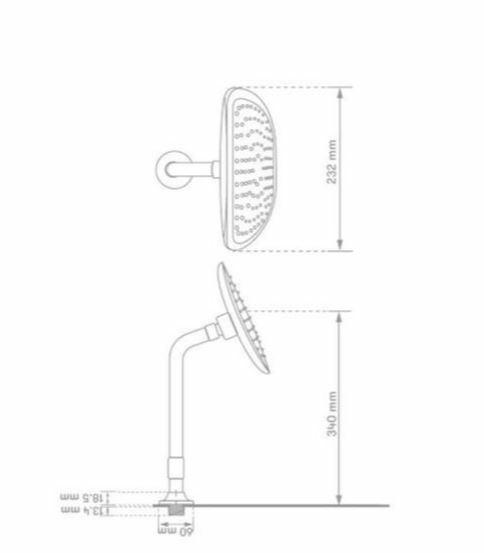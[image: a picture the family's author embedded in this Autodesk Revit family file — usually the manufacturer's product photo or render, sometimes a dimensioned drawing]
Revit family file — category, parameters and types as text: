
# Revit family: 01-2201-11 DUCHA MONOMANDO SIN SALIDA TIFFANY
name_source: partatom
category: Plumbing Fixtures
revit_build: Autodesk Revit 2018 (Build: 20170223_1515(x64)
units: mm (PartAtom-declared; Revit-internal decimal feet)

## family parameters
Cut with Voids When Loaded = No
Host = Face
OmniClass Number = 23.31.11.00
Part Type = Normal
Room Calculation Point = No
Round Connector Dimension = Use Diameter
Shared = No

## types (1)
- 01-2201-11
    Alto ducha a eje = 360 mm  [stored 1.1811 ft]
    Ancho ducha = 230 mm  [stored 0.754593 ft]
    CW Connection = Yes
    Default Elevation = 0 mm  [stored 0 ft]
    Description = Monomando ducha
    Dim escudo ducha = 65 mm  [stored 0.213255 ft]
    Dim escudo manija = 180 mm  [stored 0.590551 ft]
    HW Connection = Yes
    Link Ficha Tecnica = No encontrada en internet
    Manufacturer = Gricol
    Metal Laton Cromado = Metal Laton Cromado
    Model = 01-2201-11
    Plastico ABS Cromado = Plastico - ABS Cromado
    Product Name = DUCHA MONOMANDO SIN SALIDA TIFFANY
    Type Image = LOGO-01.jpg
    URL = https://www.gricol.com
    Vent Connection = No
    Waste Connection = No

note: [stored X ft] marks values corroborated as IEEE doubles in the binary element streams (Revit-internal decimal feet)

## geometry (parser evidence)
native form markers: Blend x4, Sweep x29
no freeform markers — native parametric forms only
